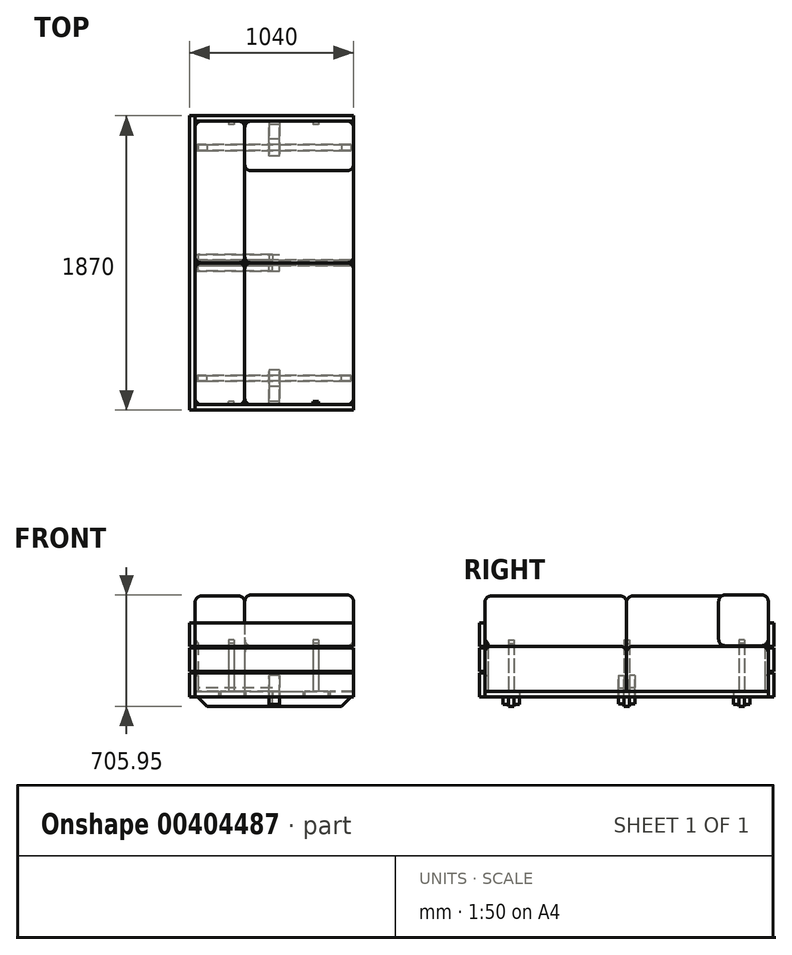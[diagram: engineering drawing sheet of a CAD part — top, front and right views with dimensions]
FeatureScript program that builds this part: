
annotation { "Feature Type Name" : "Feature", "Feature Type Description" : "" }
export const myFeature = defineFeature(function(context is Context, id is Id, definition is map)
    precondition{}
    {
        {
            var Q0;
            Q0=qCreatedBy(makeId("Front.planeOp"),FACE);
            var sketch = newSketch(context, id + "F0", { "sketchPlane" : qUnion([Q0])});
            skLineSegment(sketch, "E0.bottom", {"start": v(35, 530) * mm, "end": v(1040, 530) * mm});
            skLineSegment(sketch, "E0.top", {"start": v(35, 380) * mm, "end": v(1040, 380) * mm});
            skLineSegment(sketch, "E0.right", {"start": v(1040, 530) * mm, "end": v(1040, 380) * mm});
            skLineSegment(sketch, "E1.bottom", {"start": v(35, 370) * mm, "end": v(1040, 370) * mm});
            skLineSegment(sketch, "E1.top", {"start": v(35, 220) * mm, "end": v(1040, 220) * mm});
            skLineSegment(sketch, "E1.left", {"start": v(35, 370) * mm, "end": v(35, 220) * mm});
            skLineSegment(sketch, "E1.right", {"start": v(1040, 370) * mm, "end": v(1040, 220) * mm});
            skLineSegment(sketch, "E2.bottom", {"start": v(35, 210) * mm, "end": v(1040, 210) * mm});
            skLineSegment(sketch, "E2.top", {"start": v(35, 60) * mm, "end": v(1040, 60) * mm});
            skLineSegment(sketch, "E2.left", {"start": v(35, 210) * mm, "end": v(35, 60) * mm});
            skLineSegment(sketch, "E2.right", {"start": v(1040, 210) * mm, "end": v(1040, 60) * mm});
            skLineSegment(sketch, "E3", {"start": v(35, 380) * mm, "end": v(35, 530) * mm});
            skSolve(sketch);
        }
        {
            var Q0;
            Q0 = qSketchRegion(id + "F0", true);
            extrude(context, id + "F1", {"entities" : qUnion([Q0]), "depth" : 935 * mm, "hasSecondDirection" : true, "secondDirectionOppositeDirection" : false, "secondDirectionDepth" : 900 * mm});
        }
        {
            var Q0;
            Q0 = qSketchRegion(id + "F0", true);
            extrude(context, id + "F2", {"entities" : qUnion([Q0]), "oppositeDirection" : true, "depth" : 935 * mm, "hasSecondDirection" : true, "secondDirectionOppositeDirection" : true, "secondDirectionDepth" : 900 * mm});
        }
        {
            var Q0;
            Q0=qCreatedBy(makeId("Top.planeOp"),FACE);
            var sketch = newSketch(context, id + "F3", { "sketchPlane" : qUnion([Q0])});
            skLineSegment(sketch, "E4.bottom", {"start": v(1040, -900) * mm, "end": v(890, -900) * mm});
            skLineSegment(sketch, "E4.top", {"start": v(1040, 900) * mm, "end": v(890, 900) * mm});
            skLineSegment(sketch, "E4.left", {"start": v(1040, -900) * mm, "end": v(1040, 900) * mm});
            skLineSegment(sketch, "E4.right", {"start": v(890, -900) * mm, "end": v(890, 900) * mm});
            skLineSegment(sketch, "E5.bottom", {"start": v(880, -900) * mm, "end": v(730, -900) * mm});
            skLineSegment(sketch, "E5.top", {"start": v(880, 900) * mm, "end": v(730, 900) * mm});
            skLineSegment(sketch, "E5.left", {"start": v(880, -900) * mm, "end": v(880, 900) * mm});
            skLineSegment(sketch, "E5.right", {"start": v(730, -900) * mm, "end": v(730, 900) * mm});
            skLineSegment(sketch, "E6.bottom", {"start": v(505, -900) * mm, "end": v(355, -900) * mm});
            skLineSegment(sketch, "E6.top", {"start": v(505, 900) * mm, "end": v(355, 900) * mm});
            skLineSegment(sketch, "E6.left", {"start": v(505, -900) * mm, "end": v(505, 900) * mm});
            skLineSegment(sketch, "E6.right", {"start": v(355, -900) * mm, "end": v(355, 900) * mm});
            skLineSegment(sketch, "E7.bottom", {"start": v(345, -900) * mm, "end": v(195, -900) * mm});
            skLineSegment(sketch, "E7.top", {"start": v(345, 900) * mm, "end": v(195, 900) * mm});
            skLineSegment(sketch, "E7.left", {"start": v(345, -900) * mm, "end": v(345, 900) * mm});
            skLineSegment(sketch, "E7.right", {"start": v(195, -900) * mm, "end": v(195, 900) * mm});
            skLineSegment(sketch, "E8.bottom", {"start": v(185, -900) * mm, "end": v(35, -900) * mm});
            skLineSegment(sketch, "E8.top", {"start": v(185, 900) * mm, "end": v(35, 900) * mm});
            skLineSegment(sketch, "E8.left", {"start": v(185, -900) * mm, "end": v(185, 900) * mm});
            skLineSegment(sketch, "E8.right", {"start": v(35, 900) * mm, "end": v(35, -900) * mm});
            skLineSegment(sketch, "E9.bottom", {"start": v(570, 900) * mm, "end": v(720, 900) * mm});
            skLineSegment(sketch, "E9.top", {"start": v(570, -900) * mm, "end": v(720, -900) * mm});
            skLineSegment(sketch, "E9.left", {"start": v(570, 900) * mm, "end": v(570, -900) * mm});
            skLineSegment(sketch, "E9.right", {"start": v(720, 900) * mm, "end": v(720, -900) * mm});
            skSolve(sketch);
        }
        {
            var Q0;
            Q0 = qSketchRegion(id + "F3", true);
            extrude(context, id + "F4", {"entities" : qUnion([Q0]), "depth" : 95 * mm, "hasSecondDirection" : true, "secondDirectionOppositeDirection" : false, "secondDirectionDepth" : 60 * mm});
        }
        {
            var Q0;
            Q0=qCreatedBy(makeId("Right.planeOp"),FACE);
            var sketch = newSketch(context, id + "F5", { "sketchPlane" : qUnion([Q0])});
            skLineSegment(sketch, "E10.bottom", {"start": v(935, 530) * mm, "end": v(-935, 530) * mm});
            skLineSegment(sketch, "E10.top", {"start": v(935, 380) * mm, "end": v(-935, 380) * mm});
            skLineSegment(sketch, "E10.left", {"start": v(935, 530) * mm, "end": v(935, 380) * mm});
            skLineSegment(sketch, "E10.right", {"start": v(-935, 530) * mm, "end": v(-935, 380) * mm});
            skLineSegment(sketch, "E11.bottom", {"start": v(935, 370) * mm, "end": v(-935, 370) * mm});
            skLineSegment(sketch, "E11.top", {"start": v(935, 220) * mm, "end": v(-935, 220) * mm});
            skLineSegment(sketch, "E11.left", {"start": v(935, 370) * mm, "end": v(935, 220) * mm});
            skLineSegment(sketch, "E11.right", {"start": v(-935, 370) * mm, "end": v(-935, 220) * mm});
            skLineSegment(sketch, "E12.bottom", {"start": v(935, 210) * mm, "end": v(-935, 210) * mm});
            skLineSegment(sketch, "E12.top", {"start": v(935, 60) * mm, "end": v(-935, 60) * mm});
            skLineSegment(sketch, "E12.left", {"start": v(935, 210) * mm, "end": v(935, 60) * mm});
            skLineSegment(sketch, "E12.right", {"start": v(-935, 210) * mm, "end": v(-935, 60) * mm});
            skSolve(sketch);
        }
        {
            var Q0;
            Q0 = qSketchRegion(id + "F5", true);
            extrude(context, id + "F6", {"entities" : qUnion([Q0]), "depth" : 35 * mm});
        }
        {
            var Q0;
            Q0=qCreatedBy(makeId("Front.planeOp"),FACE);
            var sketch = newSketch(context, id + "F7", { "sketchPlane" : qUnion([Q0])});
            skLineSegment(sketch, "E13", {"start": v(50, 60) * mm, "end": v(110, 0) * mm});
            skLineSegment(sketch, "E14", {"start": v(110, 0) * mm, "end": v(965, 0) * mm});
            skLineSegment(sketch, "E15", {"start": v(965, 0) * mm, "end": v(1025, 60) * mm});
            skLineSegment(sketch, "E16", {"start": v(1025, 60) * mm, "end": v(50, 60) * mm});
            skSolve(sketch);
        }
        {
            var Q0;
            Q0=makeQuery(id+"F7.imprint","IMPRINT",FACE,{"disambiguationData":[TD([[makeQuery(id+"F7.imprint","IMPRINT",EDGE,{"derivedFrom":sQuery(id+"F7.wireOp",EDGE,"E13")}),1.0]])]});
            extrude(context, id + "F8", {"entities" : qUnion([Q0]), "depth" : 17.5 * mm, "hasSecondDirection" : true, "secondDirectionOppositeDirection" : true, "secondDirectionDepth" : 17.5 * mm});
        }
        {
            var Q0;
            Q0 = qSketchRegion(id + "F7", true);
            extrude(context, id + "F9", {"entities" : qUnion([Q0]), "depth" : 750 * mm, "hasSecondDirection" : true, "secondDirectionOppositeDirection" : false, "secondDirectionDepth" : 715 * mm});
        }
        {
            var Q0;
            Q0 = qSketchRegion(id + "F7", true);
            extrude(context, id + "F10", {"entities" : qUnion([Q0]), "oppositeDirection" : true, "depth" : 750 * mm, "hasSecondDirection" : true, "secondDirectionOppositeDirection" : true, "secondDirectionDepth" : 715 * mm});
        }
        {
            var Q0;
            Q0=qCreatedBy(makeId("Front.planeOp"),FACE);
            var sketch = newSketch(context, id + "F11", { "sketchPlane" : qUnion([Q0])});
            skLineSegment(sketch, "E17.top", {"start": v(35, 95) * mm, "end": v(55, 95) * mm});
            skLineSegment(sketch, "E17.left", {"start": v(35, 420) * mm, "end": v(35, 95) * mm});
            skLineSegment(sketch, "E17.right", {"start": v(55, 400) * mm, "end": v(55, 95) * mm});
            skLineSegment(sketch, "E18", {"start": v(35, 420) * mm, "end": v(55, 400) * mm});
            skSolve(sketch);
        }
        {
            var Q0;
            Q0 = qSketchRegion(id + "F11", true);
            extrude(context, id + "F12", {"entities" : qUnion([Q0]), "depth" : 17.5 * mm, "hasSecondDirection" : true, "secondDirectionOppositeDirection" : true, "secondDirectionDepth" : 17.5 * mm});
        }
        {
            var Q0;
            Q0 = qSketchRegion(id + "F11", true);
            extrude(context, id + "F13", {"entities" : qUnion([Q0]), "depth" : 750 * mm, "hasSecondDirection" : true, "secondDirectionOppositeDirection" : false, "secondDirectionDepth" : 715 * mm});
        }
        {
            var Q0;
            Q0 = qSketchRegion(id + "F11", true);
            extrude(context, id + "F14", {"entities" : qUnion([Q0]), "oppositeDirection" : true, "depth" : 750 * mm, "hasSecondDirection" : true, "secondDirectionOppositeDirection" : true, "secondDirectionDepth" : 715 * mm});
        }
        {
            var Q0;
            Q0=qCreatedBy(makeId("Front.planeOp"),FACE);
            var sketch = newSketch(context, id + "F15", { "sketchPlane" : qUnion([Q0])});
            skLineSegment(sketch, "E19.bottom", {"start": v(35, 195) * mm, "end": v(55, 195) * mm});
            skLineSegment(sketch, "E19.top", {"start": v(35, 95) * mm, "end": v(55, 95) * mm});
            skLineSegment(sketch, "E19.left", {"start": v(35, 95) * mm, "end": v(35, 195) * mm});
            skLineSegment(sketch, "E19.right", {"start": v(55, 145) * mm, "end": v(55, 195) * mm});
            skLineSegment(sketch, "E20.top", {"start": v(55, 95) * mm, "end": v(505, 95) * mm});
            skLineSegment(sketch, "E20.left", {"start": v(55, 145) * mm, "end": v(55, 115) * mm});
            skLineSegment(sketch, "E20.right", {"start": v(525, 115) * mm, "end": v(525, 95) * mm});
            skLineSegment(sketch, "E21.top", {"start": v(505, 15) * mm, "end": v(525, 15) * mm});
            skLineSegment(sketch, "E21.left", {"start": v(505, 95) * mm, "end": v(505, 15) * mm});
            skLineSegment(sketch, "E22", {"start": v(525, 115) * mm, "end": v(55, 115) * mm});
            skLineSegment(sketch, "E23", {"start": v(525, 15) * mm, "end": v(525, 95) * mm});
            skSolve(sketch);
        }
        {
            var Q0;
            Q0 = qSketchRegion(id + "F15", true);
            extrude(context, id + "F16", {"entities" : qUnion([Q0]), "depth" : 52.5 * mm, "hasSecondDirection" : true, "secondDirectionOppositeDirection" : false, "secondDirectionDepth" : 17.5 * mm});
        }
        {
            var Q0;
            Q0 = qSketchRegion(id + "F15", true);
            extrude(context, id + "F17", {"entities" : qUnion([Q0]), "oppositeDirection" : true, "depth" : 52.5 * mm, "hasSecondDirection" : true, "secondDirectionOppositeDirection" : true, "secondDirectionDepth" : 17.5 * mm});
        }
        {
            var Q0;
            Q0=qCreatedBy(makeId("Front.planeOp"),FACE);
            var sketch = newSketch(context, id + "F18", { "sketchPlane" : qUnion([Q0])});
            skLineSegment(sketch, "E24.bottom", {"start": v(525, 95) * mm, "end": v(570, 95) * mm});
            skLineSegment(sketch, "E24.top", {"start": v(525, 60) * mm, "end": v(570, 60) * mm});
            skLineSegment(sketch, "E24.left", {"start": v(525, 95) * mm, "end": v(525, 60) * mm});
            skLineSegment(sketch, "E24.right", {"start": v(570, 95) * mm, "end": v(570, 60) * mm});
            skSolve(sketch);
        }
        {
            var Q0;
            Q0=makeQuery(id+"F18.imprint","IMPRINT",FACE,{"disambiguationData":[TD([[makeQuery(id+"F18.imprint","IMPRINT",EDGE,{"derivedFrom":sQuery(id+"F18.wireOp",EDGE,"E24.bottom")}),-1.0]])]});
            extrude(context, id + "F19", {"entities" : qUnion([Q0]), "depth" : 52.5 * mm, "hasSecondDirection" : true, "secondDirectionOppositeDirection" : true, "secondDirectionDepth" : 52.5 * mm});
        }
        {
            var Q0;
            Q0=qCreatedBy(makeId("Right.planeOp"),FACE);
            var sketch = newSketch(context, id + "F20", { "sketchPlane" : qUnion([Q0])});
            skLineSegment(sketch, "E25.top", {"start": v(-900, 95) * mm, "end": v(-880, 95) * mm});
            skLineSegment(sketch, "E25.left", {"start": v(-900, 420) * mm, "end": v(-900, 95) * mm});
            skLineSegment(sketch, "E25.right", {"start": v(-880, 400) * mm, "end": v(-880, 95) * mm});
            skLineSegment(sketch, "E26", {"start": v(-900, 420) * mm, "end": v(-880, 400) * mm});
            skSolve(sketch);
        }
        {
            var Q0;
            Q0 = qSketchRegion(id + "F20", true);
            extrude(context, id + "F21", {"entities" : qUnion([Q0]), "depth" : 282.5 * mm, "hasSecondDirection" : true, "secondDirectionOppositeDirection" : false, "secondDirectionDepth" : 247.5 * mm});
        }
        {
            var Q0;
            Q0 = qSketchRegion(id + "F20", true);
            extrude(context, id + "F22", {"entities" : qUnion([Q0]), "depth" : 817.5 * mm, "hasSecondDirection" : true, "secondDirectionOppositeDirection" : false, "secondDirectionDepth" : 782.5 * mm});
        }
        {
            var Q0;
            Q0=qCreatedBy(makeId("Right.planeOp"),FACE);
            var sketch = newSketch(context, id + "F23", { "sketchPlane" : qUnion([Q0])});
            skLineSegment(sketch, "E27", {"start": v(-900, 60) * mm, "end": v(-900, 195) * mm});
            skLineSegment(sketch, "E28", {"start": v(-900, 195) * mm, "end": v(-880, 195) * mm});
            skLineSegment(sketch, "E29", {"start": v(-880, 195) * mm, "end": v(-880, 95) * mm});
            skLineSegment(sketch, "E30", {"start": v(-880, 95) * mm, "end": v(-680, 95) * mm});
            skLineSegment(sketch, "E31", {"start": v(-680, 95) * mm, "end": v(-680, 10) * mm});
            skLineSegment(sketch, "E32", {"start": v(-680, 10) * mm, "end": v(-715, 10) * mm});
            skLineSegment(sketch, "E33", {"start": v(-715, 10) * mm, "end": v(-715, 60) * mm});
            skLineSegment(sketch, "E34", {"start": v(-715, 60) * mm, "end": v(-750, 60) * mm});
            skLineSegment(sketch, "E35", {"start": v(-750, 60) * mm, "end": v(-750, 10) * mm});
            skLineSegment(sketch, "E36", {"start": v(-750, 10) * mm, "end": v(-785, 10) * mm});
            skLineSegment(sketch, "E37", {"start": v(-785, 10) * mm, "end": v(-785, 60) * mm});
            skLineSegment(sketch, "E38", {"start": v(-785, 60) * mm, "end": v(-900, 60) * mm});
            skSolve(sketch);
        }
        {
            var Q0;
            Q0 = qSketchRegion(id + "F23", true);
            extrude(context, id + "F24", {"entities" : qUnion([Q0]), "depth" : 570 * mm, "hasSecondDirection" : true, "secondDirectionOppositeDirection" : false, "secondDirectionDepth" : 505 * mm});
        }
        {
            var Q0;
            Q0=makeQuery(id+"F22.opExtrude","SWEPT_BODY",BODY,{"disambiguationData":[OSD([sQuery(id+"F20.wireOp",EDGE,"E25.top"),sQuery(id+"F20.wireOp",EDGE,"E25.left"),sQuery(id+"F20.wireOp",EDGE,"E25.right"),sQuery(id+"F20.wireOp",EDGE,"E26")])]});
            var Q1;
            Q1=qCreatedBy(makeId("Front.planeOp"),FACE);
            mirror(context, id + "F25", {"entities" : qUnion([Q0]), "mirrorPlane" : qUnion([Q1])});
        }
        {
            var Q0;
            Q0=makeQuery(id+"F21.opExtrude","SWEPT_BODY",BODY,{"disambiguationData":[OSD([sQuery(id+"F20.wireOp",EDGE,"E25.top"),sQuery(id+"F20.wireOp",EDGE,"E25.left"),sQuery(id+"F20.wireOp",EDGE,"E25.right"),sQuery(id+"F20.wireOp",EDGE,"E26")])]});
            var Q1;
            Q1=qCreatedBy(makeId("Front.planeOp"),FACE);
            mirror(context, id + "F26", {"entities" : qUnion([Q0]), "mirrorPlane" : qUnion([Q1])});
        }
        {
            var Q0;
            Q0=makeQuery(id+"F24.opExtrude","SWEPT_BODY",BODY,{"disambiguationData":[OSD([sQuery(id+"F23.wireOp",EDGE,"E27"),sQuery(id+"F23.wireOp",EDGE,"E28"),sQuery(id+"F23.wireOp",EDGE,"E29"),sQuery(id+"F23.wireOp",EDGE,"E30"),sQuery(id+"F23.wireOp",EDGE,"E31"),sQuery(id+"F23.wireOp",EDGE,"E32"),sQuery(id+"F23.wireOp",EDGE,"E33"),sQuery(id+"F23.wireOp",EDGE,"E34"),sQuery(id+"F23.wireOp",EDGE,"E35"),sQuery(id+"F23.wireOp",EDGE,"E36"),sQuery(id+"F23.wireOp",EDGE,"E37"),sQuery(id+"F23.wireOp",EDGE,"E38")])]});
            var Q1;
            Q1=qCreatedBy(makeId("Front.planeOp"),FACE);
            mirror(context, id + "F27", {"entities" : qUnion([Q0]), "mirrorPlane" : qUnion([Q1])});
        }
        {
            var Q0;
            Q0=qCreatedBy(makeId("Front.planeOp"),FACE);
            var sketch = newSketch(context, id + "F28", { "sketchPlane" : qUnion([Q0])});
            skLineSegment(sketch, "E39.bottom", {"start": v(390, 380) * mm, "end": v(1000, 380) * mm});
            skLineSegment(sketch, "E39.top", {"start": v(350, 95) * mm, "end": v(1040, 95) * mm});
            skLineSegment(sketch, "E39.left", {"start": v(350, 340) * mm, "end": v(350, 95) * mm});
            skLineSegment(sketch, "E39.right", {"start": v(1040, 340) * mm, "end": v(1040, 95) * mm});
            skPoint(sketch, "E40.visualSharp", {"position": v(1040, 380) * mm});
            skArc(sketch, "E40.filletArc", {"start": v(1040, 340) * mm, "mid": v(1028.28, 368.28) * mm, "end": v(1000, 380) * mm});
            skPoint(sketch, "E41.visualSharp", {"position": v(350, 380) * mm});
            skArc(sketch, "E41.filletArc", {"start": v(390, 380) * mm, "mid": v(361.72, 368.28) * mm, "end": v(350, 340) * mm});
            skSolve(sketch);
        }
        {
            var Q0;
            Q0 = qSketchRegion(id + "F28", true);
            extrude(context, id + "F29", {"entities" : qUnion([Q0]), "depth" : 900 * mm});
        }
        {
            var Q0;
            Q0=makeQuery(id+"F29.opExtrude","CAP_EDGE",EDGE,{"disambiguationData":[OSD([sQuery(id+"F28.wireOp",EDGE,"E39.bottom")])],"isStart":true});
            fillet(context, id + "F30", {"entities" : qUnion([Q0]), "radius" : 40 * mm, "tangentPropagation" : true, "allowEdgeOverflow" : false});
        }
        {
            var Q0;
            Q0=makeQuery(id+"F29.opExtrude","CAP_EDGE",EDGE,{"disambiguationData":[OSD([sQuery(id+"F28.wireOp",EDGE,"E39.bottom")])],"isStart":false});
            fillet(context, id + "F31", {"entities" : qUnion([Q0]), "radius" : 40 * mm, "tangentPropagation" : true, "allowEdgeOverflow" : false});
        }
        {
            var Q0;
            Q0=makeQuery(id+"F29.opExtrude","SWEPT_BODY",BODY,{"disambiguationData":[OSD([sQuery(id+"F28.wireOp",EDGE,"E39.bottom"),sQuery(id+"F28.wireOp",EDGE,"E39.top"),sQuery(id+"F28.wireOp",EDGE,"E39.left"),sQuery(id+"F28.wireOp",EDGE,"E39.right"),sQuery(id+"F28.wireOp",EDGE,"E40.filletArc")])]});
            var Q1;
            Q1=qCreatedBy(makeId("Front.planeOp"),FACE);
            mirror(context, id + "F32", {"entities" : qUnion([Q0]), "mirrorPlane" : qUnion([Q1])});
        }
        {
            var Q0;
            Q0=qCreatedBy(makeId("Front.planeOp"),FACE);
            var sketch = newSketch(context, id + "F33", { "sketchPlane" : qUnion([Q0])});
            skLineSegment(sketch, "E42.bottom", {"start": v(75, 700) * mm, "end": v(310, 700) * mm});
            skLineSegment(sketch, "E42.top", {"start": v(35, 95) * mm, "end": v(350, 95) * mm});
            skLineSegment(sketch, "E42.left", {"start": v(35, 660) * mm, "end": v(35, 95) * mm});
            skLineSegment(sketch, "E42.right", {"start": v(350, 660) * mm, "end": v(350, 95) * mm});
            skPoint(sketch, "E43.visualSharp", {"position": v(35, 700) * mm});
            skArc(sketch, "E43.filletArc", {"start": v(75, 700) * mm, "mid": v(46.72, 688.28) * mm, "end": v(35, 660) * mm});
            skPoint(sketch, "E44.visualSharp", {"position": v(350, 700) * mm});
            skArc(sketch, "E44.filletArc", {"start": v(350, 660) * mm, "mid": v(338.28, 688.28) * mm, "end": v(310, 700) * mm});
            skSolve(sketch);
        }
        {
            var Q0;
            Q0 = qSketchRegion(id + "F33", true);
            extrude(context, id + "F34", {"entities" : qUnion([Q0]), "depth" : 900 * mm});
        }
        {
            var Q0;
            Q0=makeQuery(id+"F34.opExtrude","CAP_EDGE",EDGE,{"disambiguationData":[OSD([sQuery(id+"F33.wireOp",EDGE,"E42.right")])],"isStart":true});
            var Q1;
            Q1=makeQuery(id+"F34.opExtrude","CAP_EDGE",EDGE,{"disambiguationData":[OSD([sQuery(id+"F33.wireOp",EDGE,"E42.bottom")])],"isStart":false});
            fillet(context, id + "F35", {"entities" : qUnion([Q0, Q1]), "radius" : 40 * mm, "tangentPropagation" : true, "allowEdgeOverflow" : false});
        }
        {
            var Q0;
            Q0=makeQuery(id+"F34.opExtrude","SWEPT_BODY",BODY,{"disambiguationData":[OSD([sQuery(id+"F33.wireOp",EDGE,"E42.bottom"),sQuery(id+"F33.wireOp",EDGE,"E42.top"),sQuery(id+"F33.wireOp",EDGE,"E42.left"),sQuery(id+"F33.wireOp",EDGE,"E42.right"),sQuery(id+"F33.wireOp",EDGE,"E43.filletArc"),sQuery(id+"F33.wireOp",EDGE,"E44.filletArc")])]});
            var Q1;
            Q1=qCreatedBy(makeId("Front.planeOp"),FACE);
            mirror(context, id + "F36", {"entities" : qUnion([Q0]), "mirrorPlane" : qUnion([Q1])});
        }
        {
            var Q0;
            Q0=qCreatedBy(makeId("Right.planeOp"),FACE);
            var sketch = newSketch(context, id + "F37", { "sketchPlane" : qUnion([Q0])});
            skLineSegment(sketch, "E45.bottom", {"start": v(625, 705.95) * mm, "end": v(860, 705.95) * mm});
            skLineSegment(sketch, "E45.top", {"start": v(625, 384.52) * mm, "end": v(860, 384.52) * mm});
            skLineSegment(sketch, "E45.left", {"start": v(585, 665.95) * mm, "end": v(585, 424.52) * mm});
            skLineSegment(sketch, "E45.right", {"start": v(900, 665.95) * mm, "end": v(900, 424.52) * mm});
            skPoint(sketch, "E46.visualSharp", {"position": v(585, 705.95) * mm});
            skArc(sketch, "E46.filletArc", {"start": v(625, 705.95) * mm, "mid": v(596.72, 694.23) * mm, "end": v(585, 665.95) * mm});
            skPoint(sketch, "E47.visualSharp", {"position": v(900, 705.95) * mm});
            skArc(sketch, "E47.filletArc", {"start": v(900, 665.95) * mm, "mid": v(888.28, 694.23) * mm, "end": v(860, 705.95) * mm});
            skPoint(sketch, "E48.visualSharp", {"position": v(585, 384.52) * mm});
            skArc(sketch, "E48.filletArc", {"start": v(585, 424.52) * mm, "mid": v(596.72, 396.23) * mm, "end": v(625, 384.52) * mm});
            skPoint(sketch, "E49.visualSharp", {"position": v(900, 384.52) * mm});
            skArc(sketch, "E49.filletArc", {"start": v(860, 384.52) * mm, "mid": v(888.28, 396.23) * mm, "end": v(900, 424.52) * mm});
            skSolve(sketch);
        }
        {
            var Q0;
            Q0=makeQuery(id+"F37.imprint","IMPRINT",FACE,{"disambiguationData":[TD([[makeQuery(id+"F37.imprint","IMPRINT",EDGE,{"derivedFrom":sQuery(id+"F37.wireOp",EDGE,"E45.bottom")}),-1.0]])]});
            extrude(context, id + "F38", {"entities" : qUnion([Q0]), "depth" : 1040 * mm, "hasSecondDirection" : true, "secondDirectionOppositeDirection" : false, "secondDirectionDepth" : 350 * mm});
        }
        {
            var Q0;
            Q0=makeQuery(id+"F38.opExtrude","CAP_EDGE",EDGE,{"disambiguationData":[OSD([sQuery(id+"F37.wireOp",EDGE,"E45.left")])],"isStart":false});
            fillet(context, id + "F39", {"entities" : qUnion([Q0]), "radius" : 40 * mm, "tangentPropagation" : true, "allowEdgeOverflow" : false});
        }
        {
            var Q0;
            Q0=makeQuery(id+"F38.opExtrude","CAP_EDGE",EDGE,{"disambiguationData":[OSD([sQuery(id+"F37.wireOp",EDGE,"E46.filletArc")])],"isStart":true});
            fillet(context, id + "F40", {"entities" : qUnion([Q0]), "radius" : 40 * mm, "tangentPropagation" : true, "allowEdgeOverflow" : false});
        }
    });
